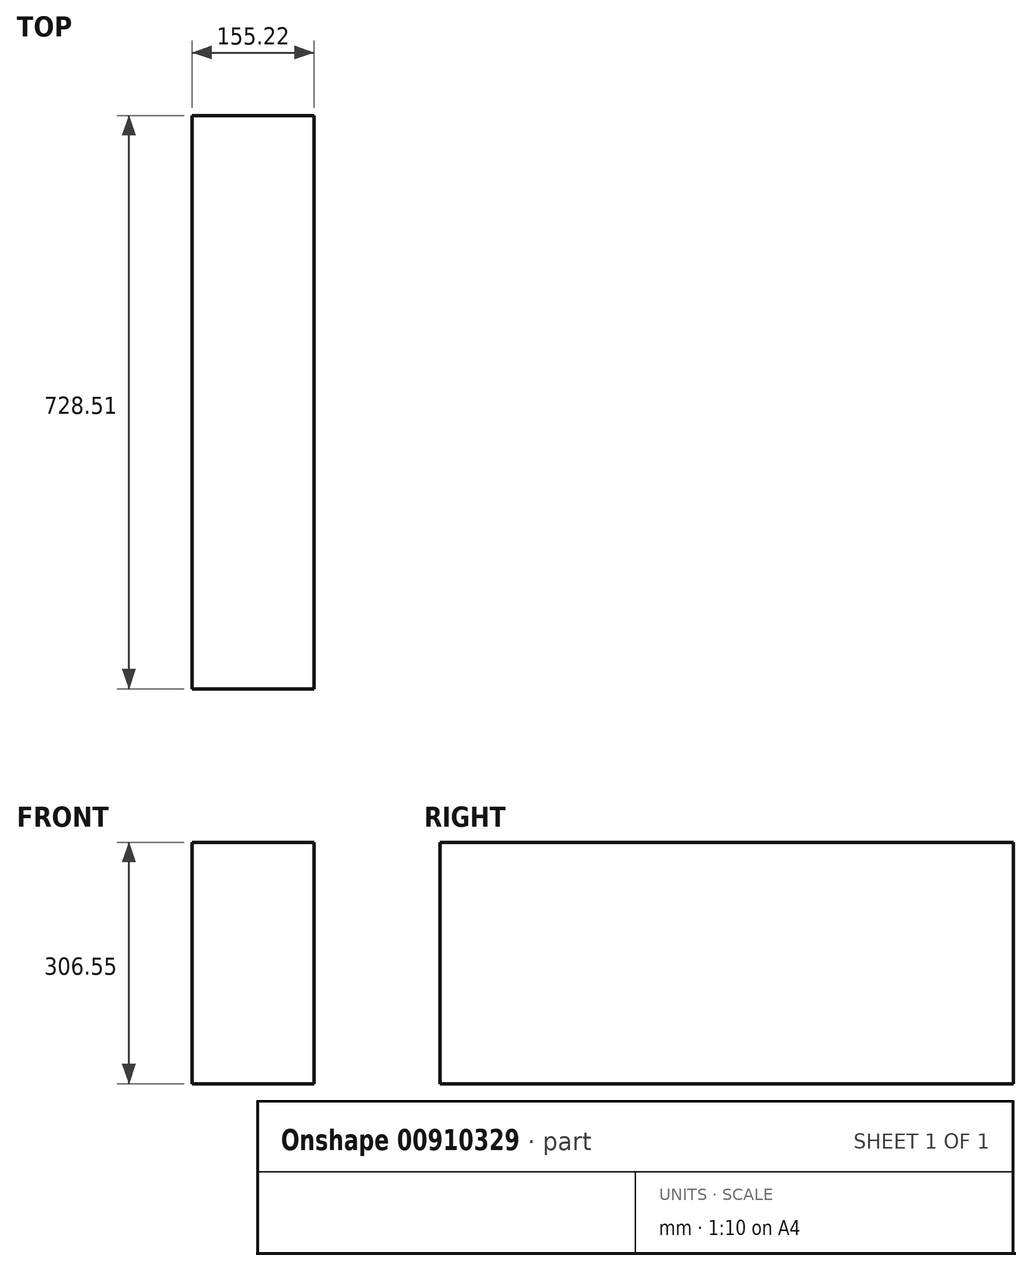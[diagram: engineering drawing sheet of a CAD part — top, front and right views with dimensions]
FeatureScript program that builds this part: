
annotation { "Feature Type Name" : "Feature", "Feature Type Description" : "" }
export const myFeature = defineFeature(function(context is Context, id is Id, definition is map)
    precondition{}
    {
        {
            var Q0;
            Q0=qCreatedBy(makeId("Right.planeOp"),FACE);
            var sketch = newSketch(context, id + "F0", { "sketchPlane" : qUnion([Q0])});
            skLineSegment(sketch, "E0.bottom", {"start": v(728.5, -252.35) * mm, "end": v(0, -252.35) * mm});
            skLineSegment(sketch, "E0.top", {"start": v(728.5, 54.2) * mm, "end": v(0, 54.2) * mm});
            skLineSegment(sketch, "E0.left", {"start": v(728.5, -252.35) * mm, "end": v(728.5, 54.2) * mm});
            skLineSegment(sketch, "E0.right", {"start": v(0, -252.35) * mm, "end": v(0, 54.2) * mm});
            skSolve(sketch);
        }
        {
            var Q0;
            Q0 = qSketchRegion(id + "F0", true);
            extrude(context, id + "F1", {"entities" : qUnion([Q0]), "depth" : 155.22 * mm, "offsetDistance" : 25.4 * mm});
        }
        {
            var Q0;
            Q0=makeQuery(id+"F1.opExtrude","CAP_FACE",FACE,{"disambiguationData":[OSD([sQuery(id+"F0.wireOp",EDGE,"E0.bottom"),sQuery(id+"F0.wireOp",EDGE,"E0.top"),sQuery(id+"F0.wireOp",EDGE,"E0.left"),sQuery(id+"F0.wireOp",EDGE,"E0.right")])],"isStart":true});
            var sketch = newSketch(context, id + "F2", { "sketchPlane" : qUnion([Q0])});
            skCircle(sketch, "E1", {"center": v(-335.28, -123.6) * mm, "radius": 50.8 * mm});
            skSolve(sketch);
        }
        {
            var Q0;
            Q0=makeQuery(id+"F2.imprint","IMPRINT",FACE,{"disambiguationData":[TD([[makeQuery(id+"F2.imprint","IMPRINT",EDGE,{"derivedFrom":sQuery(id+"F2.wireOp",EDGE,"E1")}),1.0]])]});
            extrude(context, id + "F3", {"entities" : qUnion([Q0]), "operationType" : NewBodyOperationType.ADD, "oppositeDirection" : true, "depth" : 7.62 * mm, "offsetDistance" : 25.4 * mm});
        }
        {
            var Q0;
            Q0 = qSketchRegion(id + "F2", true);
            var Q1;
            Q1=makeQuery(id+"F1.opExtrude","CAP_FACE",FACE,{"disambiguationData":[OSD([sQuery(id+"F0.wireOp",EDGE,"E0.bottom"),sQuery(id+"F0.wireOp",EDGE,"E0.top"),sQuery(id+"F0.wireOp",EDGE,"E0.left"),sQuery(id+"F0.wireOp",EDGE,"E0.right")])],"isStart":true});
            var Q2;
            Q2=makeQuery(id+"F3.opExtrude","CAP_FACE",FACE,{"disambiguationData":[OSD([sQuery(id+"F2.wireOp",EDGE,"E1")])],"isStart":false});
            extrude(context, id + "F4", {"entities" : qUnion([Q0, Q1, Q2]), "operationType" : NewBodyOperationType.REMOVE, "endBound" : BoundingType.THROUGH_ALL, "depth" : 5.08 * mm, "offsetDistance" : 25.4 * mm});
        }
    });
